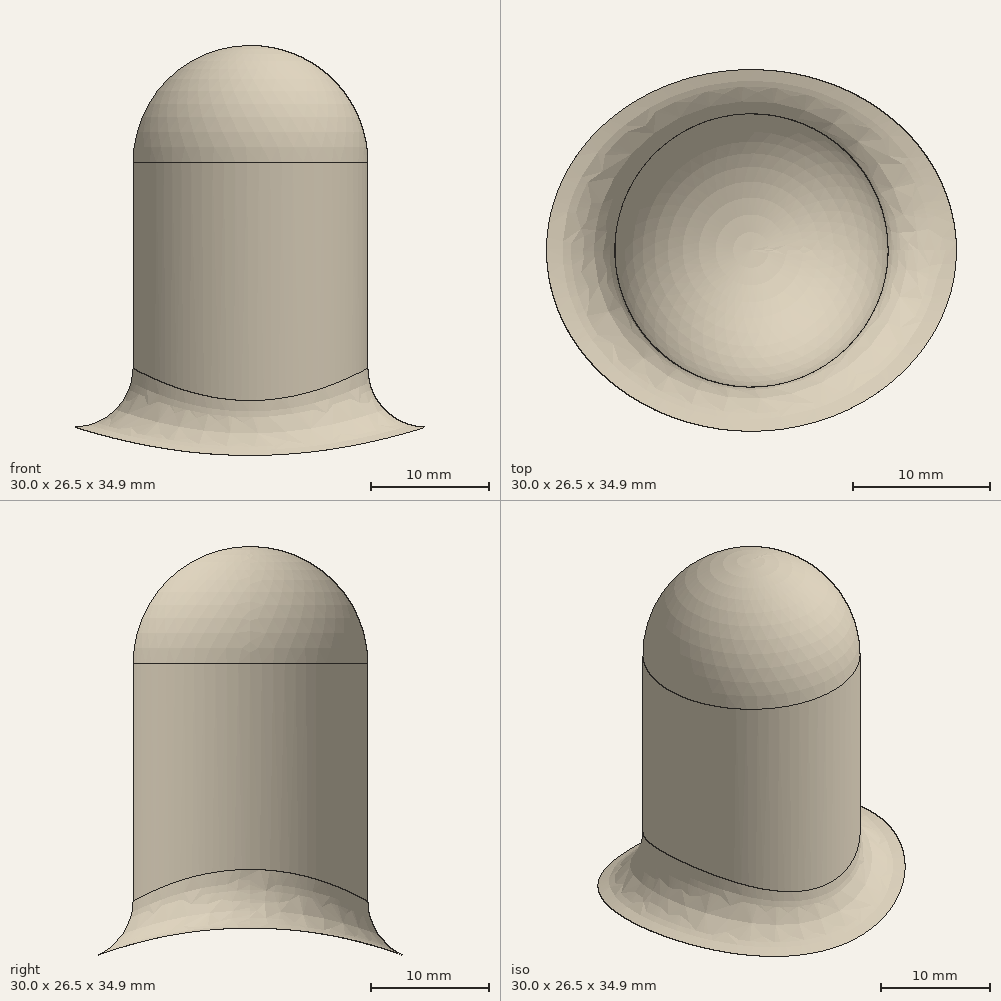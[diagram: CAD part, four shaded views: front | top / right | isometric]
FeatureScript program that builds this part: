
annotation { "Feature Type Name" : "Feature", "Feature Type Description" : "" }
export const myFeature = defineFeature(function(context is Context, id is Id, definition is map)
    precondition{}
    {
        {
            var Q0;
            Q0=qCreatedBy(makeId("Front.planeOp"),FACE);
            var sketch = newSketch(context, id + "F0", { "sketchPlane" : qUnion([Q0])});
            skLineSegment(sketch, "E0", {"start": v(0, 0) * mm, "end": v(0, 25) * mm});
            skArc(sketch, "E1", {"start": v(0, 25) * mm, "mid": v(-2.93, 32.07) * mm, "end": v(-10, 35) * mm});
            skArc(sketch, "E2.0", {"start": v(-1, 25) * mm, "mid": v(-3.64, 31.36) * mm, "end": v(-10, 34) * mm});
            skLineSegment(sketch, "E2.1", {"start": v(-1, 0) * mm, "end": v(-1, 25) * mm});
            skLineSegment(sketch, "E3", {"start": v(-1, 0) * mm, "end": v(0, 0) * mm});
            skLineSegment(sketch, "E4", {"start": v(-10, 35) * mm, "end": v(-10, 34) * mm});
            skSolve(sketch);
        }
        {
            var Q0;
            Q0 = qSketchRegion(id + "F0", true);
            var Q1;
            Q1=sQuery(id+"F0.wireOp",EDGE,"E4");
            revolve(context, id + "F1", {"entities" : qUnion([Q0]), "axis" : qUnion([Q1]), "revolveType" : RevolveType.FULL});
        }
        {
            var Q0;
            Q0=qCreatedBy(makeId("Right.planeOp"),FACE);
            var sketch = newSketch(context, id + "F2", { "sketchPlane" : qUnion([Q0])});
            skCircle(sketch, "E5", {"center": v(0, -35) * mm, "radius": 37.5 * mm});
            skSolve(sketch);
        }
        {
            var Q0;
            Q0 = qSketchRegion(id + "F2", true);
            extrude(context, id + "F3", {"entities" : qUnion([Q0]), "operationType" : NewBodyOperationType.ADD, "endBound" : BoundingType.SYMMETRIC, "oppositeDirection" : true, "depth" : 70 * mm});
        }
        {
            var Q0;
            Q0=makeQuery(id+"F3.boolean.opBoolean","INTERSECT",EDGE,{"derivedFrom":[makeQuery(id+"F1.opRevolve","SWEPT_FACE",FACE,{"disambiguationData":[OSD([sQuery(id+"F0.wireOp",EDGE,"E0")])]}),makeQuery(id+"F3.opExtrude","SWEPT_FACE",FACE,{"disambiguationData":[OSD([sQuery(id+"F2.wireOp",EDGE,"E5")])]})]});
            fillet(context, id + "F4", {"entities" : qUnion([Q0]), "radius" : 5 * mm, "tangentPropagation" : true, "allowEdgeOverflow" : false});
        }
        {
            var Q0;
            Q0=qCreatedBy(makeId("Top.planeOp"),FACE);
            var sketch = newSketch(context, id + "F5", { "sketchPlane" : qUnion([Q0])});
            skFitSpline(sketch, "E6.0", {"points": [v(5, 0) * mm, v(5, -0.23) * mm, v(4.99, -0.7) * mm, v(4.9, -1.63) * mm, v(4.7, -2.76) * mm, v(4.36, -3.87) * mm, v(4.01, -4.74) * mm, v(3.62, -5.58) * mm, v(3.05, -6.57) * mm, v(2.38, -7.5) * mm, v(1.79, -8.2) * mm, v(1.15, -8.87) * mm, v(0.3, -9.65) * mm, v(-0.8, -10.47) * mm, v(-1.97, -11.2) * mm, v(-3.22, -11.83) * mm, v(-4.5, -12.33) * mm, v(-5.83, -12.73) * mm, v(-7.67, -13.12) * mm, v(-9.29, -13.25) * mm, v(-10.68, -13.23) * mm, v(-11.62, -13.17) * mm, v(-12.78, -13.03) * mm, v(-14.13, -12.74) * mm, v(-15.46, -12.35) * mm, v(-16.77, -11.83) * mm, v(-18, -11.22) * mm, v(-19.17, -10.5) * mm, v(-20.1, -9.8) * mm, v(-20.8, -9.2) * mm, v(-21.45, -8.57) * mm, v(-22.22, -7.71) * mm, v(-22.9, -6.79) * mm, v(-23.38, -6) * mm, v(-23.82, -5.18) * mm, v(-24.28, -4.12) * mm, v(-24.69, -2.8) * mm, v(-24.94, -1.4) * mm, v(-25.03, -0.02) * mm, v(-24.95, 1.37) * mm, v(-24.7, 2.76) * mm, v(-24.3, 4.09) * mm, v(-23.74, 5.36) * mm, v(-23.05, 6.58) * mm, v(-22.23, 7.7) * mm, v(-21.32, 8.72) * mm, v(-20.3, 9.65) * mm, v(-19.2, 10.49) * mm, v(-18.02, 11.2) * mm, v(-16.99, 11.72) * mm, v(-16.14, 12.08) * mm, v(-15.26, 12.4) * mm, v(-14.15, 12.74) * mm, v(-12.79, 13.02) * mm, v(-11.63, 13.17) * mm, v(-10.7, 13.23) * mm, v(-9.3, 13.25) * mm, v(-7.91, 13.14) * mm, v(-6.54, 12.88) * mm, v(-5.62, 12.67) * mm, v(-4.51, 12.34) * mm, v(-3.23, 11.83) * mm, v(-2, 11.22) * mm, v(-0.8, 10.48) * mm, v(0.29, 9.66) * mm, v(1.13, 8.89) * mm, v(1.77, 8.22) * mm, v(2.37, 7.51) * mm, v(3.04, 6.58) * mm, v(3.62, 5.58) * mm, v(4, 4.75) * mm, v(4.27, 4.1) * mm, v(4.5, 3.43) * mm, v(4.74, 2.54) * mm, v(4.9, 1.63) * mm, v(4.99, 0.7) * mm, v(5, 0.23) * mm, v(5, 0) * mm]});
            skLineSegment(sketch, "E7.bottom", {"start": v(42.47, 56.03) * mm, "end": v(-52.14, 56.03) * mm});
            skLineSegment(sketch, "E7.top", {"start": v(42.47, -58.33) * mm, "end": v(-52.14, -58.33) * mm});
            skLineSegment(sketch, "E7.left", {"start": v(42.47, 56.03) * mm, "end": v(42.47, -58.33) * mm});
            skLineSegment(sketch, "E7.right", {"start": v(-52.14, 56.03) * mm, "end": v(-52.14, -58.33) * mm});
            skSolve(sketch);
        }
        {
            var Q0;
            Q0 = qSketchRegion(id + "F5", true);
            extrude(context, id + "F6", {"entities" : qUnion([Q0]), "operationType" : NewBodyOperationType.REMOVE, "endBound" : BoundingType.SYMMETRIC, "depth" : 200 * mm});
        }
        {
            var Q0;
            Q0=qCreatedBy(makeId("Right.planeOp"),FACE);
            var sketch = newSketch(context, id + "F7", { "sketchPlane" : qUnion([Q0])});
            skCircle(sketch, "E8", {"center": v(0, -35) * mm, "radius": 37.5 * mm});
            skSolve(sketch);
        }
        {
            var Q0;
            Q0 = qSketchRegion(id + "F7", true);
            extrude(context, id + "F8", {"entities" : qUnion([Q0]), "operationType" : NewBodyOperationType.REMOVE, "endBound" : BoundingType.SYMMETRIC, "oppositeDirection" : true, "depth" : 100 * mm});
        }
    });
